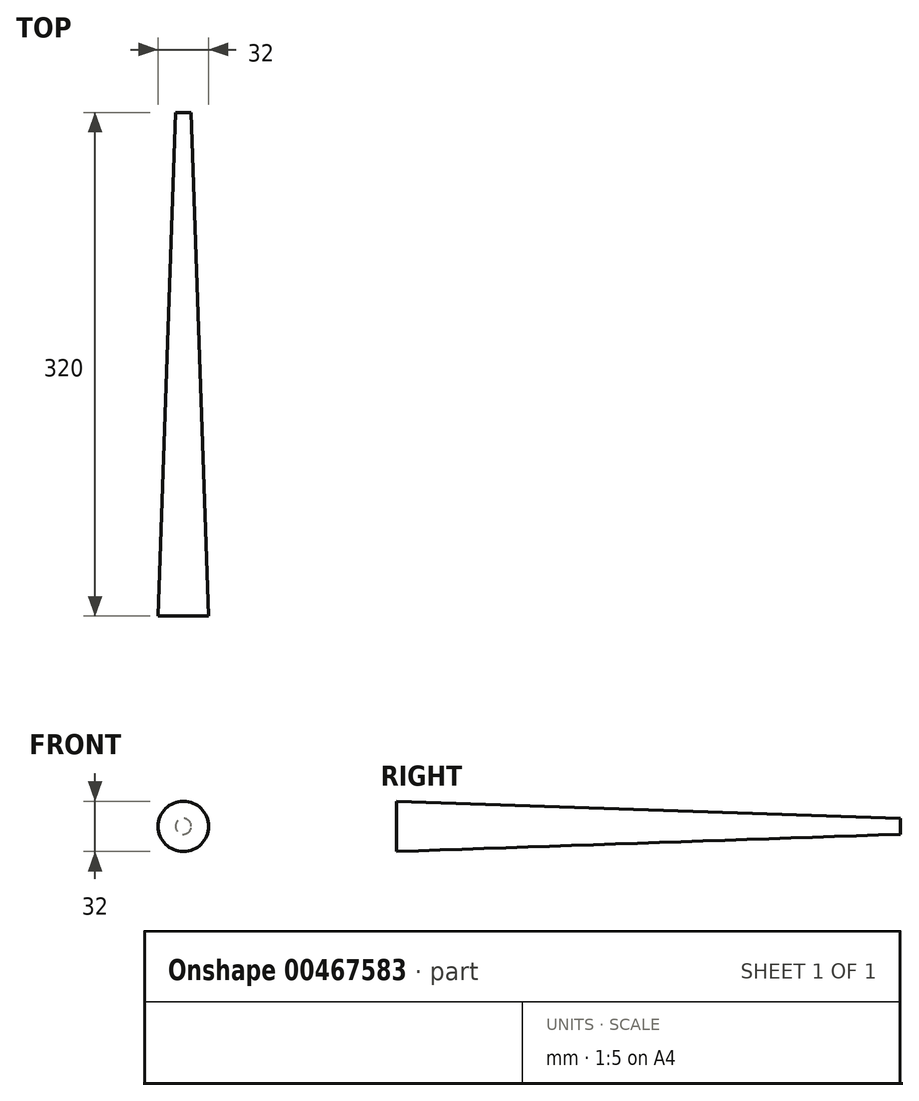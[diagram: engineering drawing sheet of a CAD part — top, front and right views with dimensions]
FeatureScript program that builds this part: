
annotation { "Feature Type Name" : "Feature", "Feature Type Description" : "" }
export const myFeature = defineFeature(function(context is Context, id is Id, definition is map)
    precondition{}
    {
        {
            var Q0;
            Q0=qCreatedBy(makeId("Top.planeOp"),FACE);
            var sketch = newSketch(context, id + "F0", { "sketchPlane" : qUnion([Q0])});
            skLineSegment(sketch, "E0", {"start": v(0, 0) * mm, "end": v(0, 320) * mm});
            skLineSegment(sketch, "E1", {"start": v(0, 0) * mm, "end": v(-16, 0) * mm});
            skLineSegment(sketch, "E2", {"start": v(-16, 0) * mm, "end": v(-5, 320) * mm});
            skLineSegment(sketch, "E3", {"start": v(-5, 320) * mm, "end": v(0, 320) * mm});
            skSolve(sketch);
        }
        {
            var Q0;
            Q0=makeQuery(id+"F0.imprint","IMPRINT",FACE,{"disambiguationData":[TD([[makeQuery(id+"F0.imprint","IMPRINT",EDGE,{"derivedFrom":sQuery(id+"F0.wireOp",EDGE,"E0")}),1.0]])]});
            var Q1;
            Q1=sQuery(id+"F0.wireOp",EDGE,"E0");
            revolve(context, id + "F1", {"entities" : qUnion([Q0]), "axis" : qUnion([Q1]), "revolveType" : RevolveType.FULL});
        }
    });
